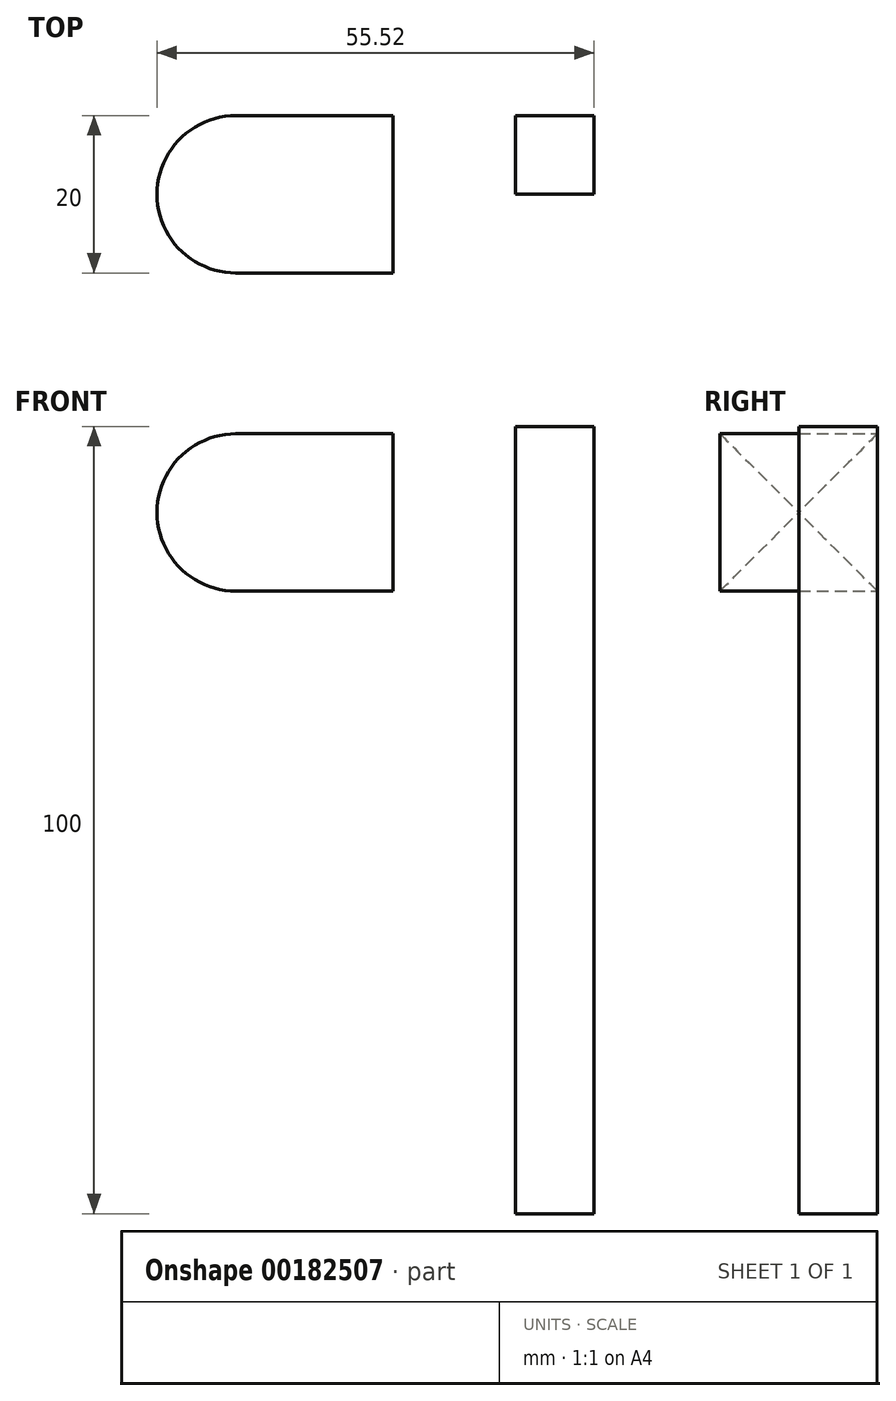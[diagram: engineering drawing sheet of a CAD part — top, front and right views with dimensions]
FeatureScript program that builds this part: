
annotation { "Feature Type Name" : "Feature", "Feature Type Description" : "" }
export const myFeature = defineFeature(function(context is Context, id is Id, definition is map)
    precondition{}
    {
        {
            var Q0;
            Q0=qCreatedBy(makeId("Front.planeOp"),FACE);
            var sketch = newSketch(context, id + "F0", { "sketchPlane" : qUnion([Q0])});
            skLineSegment(sketch, "E0.bottom", {"start": v(-10.33, 37.7) * mm, "end": v(-0.33, 37.7) * mm});
            skLineSegment(sketch, "E0.top", {"start": v(-10.33, -62.3) * mm, "end": v(-0.33, -62.3) * mm});
            skLineSegment(sketch, "E0.left", {"start": v(-10.33, 37.7) * mm, "end": v(-10.33, -62.3) * mm});
            skLineSegment(sketch, "E0.right", {"start": v(-0.33, 37.7) * mm, "end": v(-0.33, -62.3) * mm});
            skSolve(sketch);
        }
        {
            var Q0;
            Q0=makeQuery(id+"F0.imprint","IMPRINT",FACE,{"disambiguationData":[TD([[makeQuery(id+"F0.imprint","IMPRINT",EDGE,{"derivedFrom":sQuery(id+"F0.wireOp",EDGE,"E0.bottom")}),-1.0]])]});
            extrude(context, id + "F1", {"entities" : qUnion([Q0]), "depth" : 10 * mm});
        }
        {
            var Q0;
            Q0=qCreatedBy(makeId("Front.planeOp"),FACE);
            var sketch = newSketch(context, id + "F2", { "sketchPlane" : qUnion([Q0])});
            skLineSegment(sketch, "E1.bottom", {"start": v(-55.85, 36.78) * mm, "end": v(-25.85, 36.78) * mm});
            skLineSegment(sketch, "E1.top", {"start": v(-55.85, 16.78) * mm, "end": v(-25.85, 16.78) * mm});
            skLineSegment(sketch, "E1.left", {"start": v(-55.85, 36.78) * mm, "end": v(-55.85, 16.78) * mm});
            skLineSegment(sketch, "E1.right", {"start": v(-25.85, 36.78) * mm, "end": v(-25.85, 16.78) * mm});
            skSolve(sketch);
        }
        {
            var Q0;
            Q0 = qSketchRegion(id + "F2", true);
            extrude(context, id + "F3", {"entities" : qUnion([Q0]), "depth" : 20 * mm});
        }
        {
            var Q0;
            Q0=makeQuery(id+"F3.opExtrude","SWEPT_FACE",FACE,{"disambiguationData":[OSD([sQuery(id+"F2.wireOp",EDGE,"E1.left")])]});
            fillet(context, id + "F4", {"entities" : qUnion([Q0]), "radius" : 10 * mm, "tangentPropagation" : true, "allowEdgeOverflow" : false});
        }
    });
